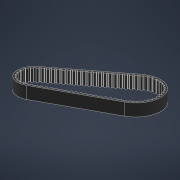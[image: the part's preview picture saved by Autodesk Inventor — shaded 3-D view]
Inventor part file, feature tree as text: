
AUTODESK INVENTOR PART (.ipt)
format: ipt  version: 2021 (Build 250183000, 183)  size: 928,768 bytes
history: native  units: in
note: dims shown in document units (in); Inventor stores cm internally (conversion verified against a paired STEP export)
features: other x7, extrude x4, pattern_circular x2, sketch x1
ambient origin geometry x8: Origin, YZ Plane, XZ Plane, XY Plane, X Axis, Y Axis, Z Axis, Center Point
bodies: Body1 (feature_tree)
feature tree (14):
  other  "top teeth placement"
  other  "gt2 profile"
  extrude  "Top/Left Base Tooth"  Depth=0.3543in
  other  "Top Teeth"
  other  "Pulley 1 Center"
  pattern_circular  "Left Teeth"  Count=21  [1 undecoded]
  other  "Pulley 2 Center"
  extrude  "Right Base Tooth"  Depth=0.3543in
  pattern_circular  "Right Teeth"  [2 undecoded]
  other  "bottom teeth placement"
  extrude  "Bottom Base Tooth"  Depth=0.3543in TaperAngle=15.0deg
  other  "Bottom Teeth"
  extrude  "Extrusion7"  Depth=0.3543in
  sketch  "Sketch8"  dims[d17=0.9023in d18=1.3534in d28=8.2677in d30=0.1181in d31=0.3937in d33=0.3937in d35=2.3405in d36=1.3306in d37=0.7874in d39=15.0deg d41=0.1181in d43=0.0394in d44=0.1398in d45=2.256in d46=0.7874in d48=0.0687in d50=0.1181in d52=0.0867in d60=0.7874in d62=0.1181in d63=0.3937in d65=0.3937in d71=2.3514in d74=0.3543in d75=0.0in d76=4.3307in d77=165.0deg d80=1.3605in d81=1.3193in d85=0.3543in d86=0.0in d87=7.4803in d88=180.0deg d108=0.1969in d120=7.874in d122=0.3937in d123=0.9023in d124=1.3534in d126=2.3405in d127=1.3306in d131=2.256in d134=0.0867in d135=0.1181in d136=2.3514in d140=0.3937in d144=0.1181in d145=9.4488in d146=14.1732in d147=1.2992in d156=0.1969in d158=0.3543in d159=0.0in d165=0.0598in d170=0.0335in d171=0.0598in d172=0.0098in d173=0.015in d175=0.0244in d176=0.0598in d177=0.0394in d178=0.0449in d185=0.0335in d186=0.0098in d187=0.0244in d188=0.0598in d189=0.0394in d190=0.0449in d192=0.015in d193=0.0867in d194=0.0335in d195=0.0098in d196=0.0244in d197=0.0598in d198=0.0394in d199=0.0449in d200=0.015in d201=0.015in d202=0.0496in d203=0.3543in d204=0.0in d111=0.0197in d112=0.0344in d113=0.0197in d114=0.0344in]
note: 3 required parameter values undecoded (feature->parameter linkage not recoverable at this tier; creation-order binding heuristic only, values carry confidence <= 0.55)
